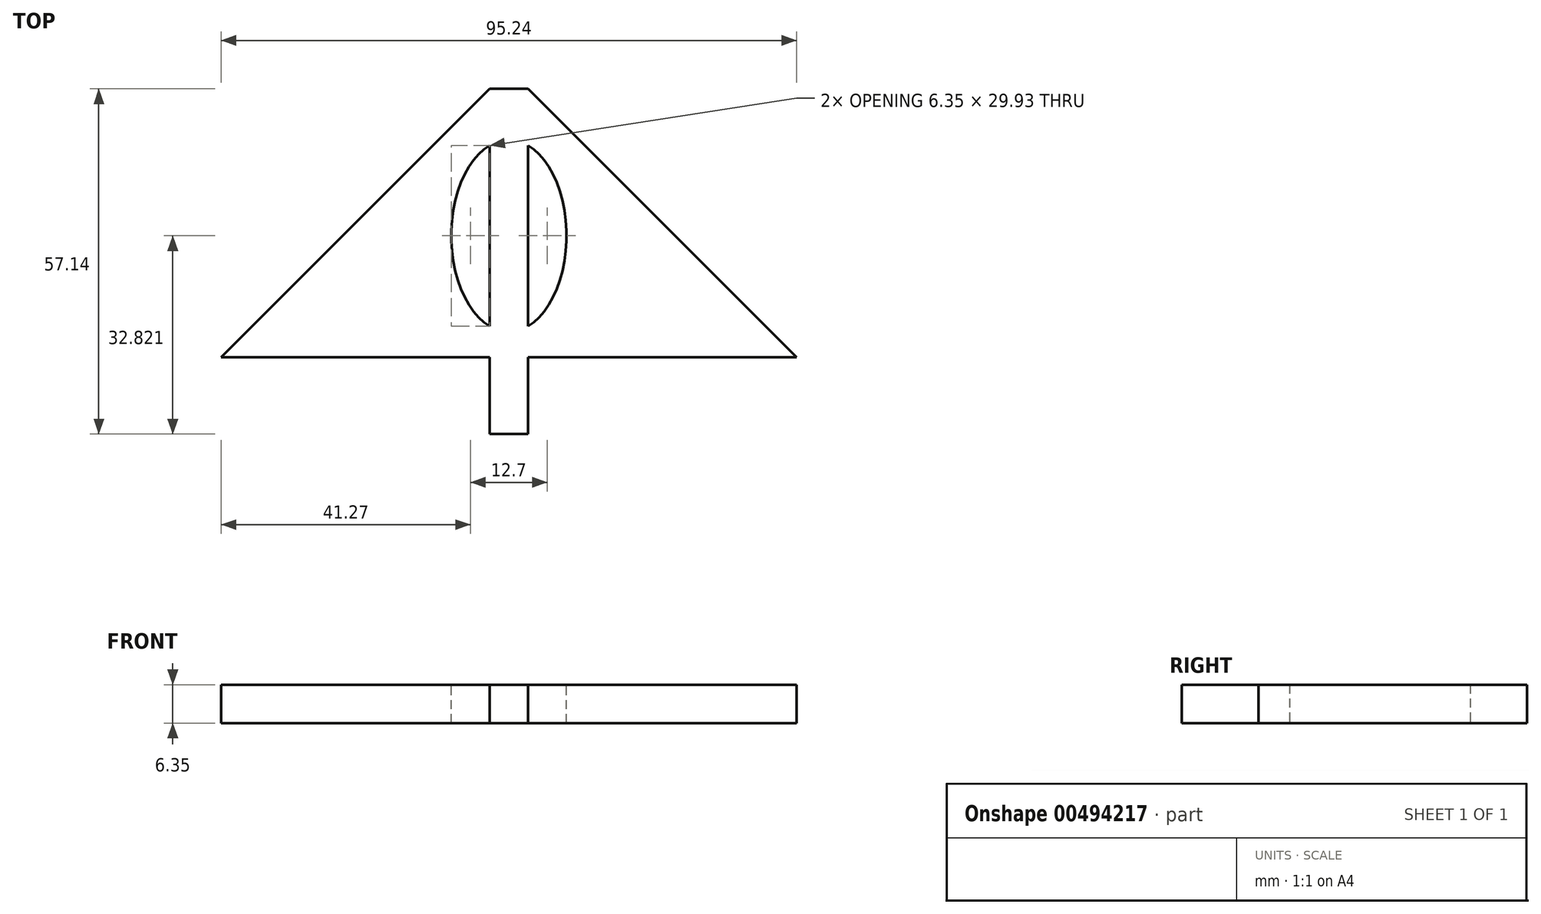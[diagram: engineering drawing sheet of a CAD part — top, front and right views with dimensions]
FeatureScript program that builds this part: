
annotation { "Feature Type Name" : "Feature", "Feature Type Description" : "" }
export const myFeature = defineFeature(function(context is Context, id is Id, definition is map)
    precondition{}
    {
        {
            var Q0;
            Q0=qCreatedBy(makeId("Top.planeOp"),FACE);
            var sketch = newSketch(context, id + "F0", { "sketchPlane" : qUnion([Q0])});
            skLineSegment(sketch, "E0.bottom", {"start": v(3.18, 28.58) * mm, "end": v(-3.17, 28.58) * mm});
            skLineSegment(sketch, "E0.top", {"start": v(3.17, -28.58) * mm, "end": v(-3.18, -28.58) * mm});
            skLineSegment(sketch, "E0.left", {"start": v(3.18, 28.58) * mm, "end": v(3.17, -28.58) * mm});
            skLineSegment(sketch, "E0.right", {"start": v(-3.17, 28.58) * mm, "end": v(-3.18, -28.58) * mm});
            skPoint(sketch, "E0.middle", {"position": v(0, 0) * mm});
            skLineSegment(sketch, "E1", {"start": v(-3.17, -15.87) * mm, "end": v(-47.62, -15.88) * mm});
            skLineSegment(sketch, "E2", {"start": v(-47.62, -15.88) * mm, "end": v(-3.17, 28.58) * mm});
            skLineSegment(sketch, "E3", {"start": v(3.18, -15.88) * mm, "end": v(47.62, -15.88) * mm});
            skLineSegment(sketch, "E4", {"start": v(47.62, -15.87) * mm, "end": v(3.18, 28.58) * mm});
            skEllipse(sketch, "E5", {"center": v(0, 4.25) * mm, "majorRadius": 15.88 * mm, "minorRadius": 9.53 * mm, "majorAxis": v(0, 1)});
            skSolve(sketch);
        }
        {
            var Q0;
            {var subQ0=sQuery(id+"F0.wireOp",EDGE,"E1");Q0=makeQuery(id+"F0.imprint","IMPRINT",FACE,{"disambiguationData":[TD([[makeQuery(id+"F0.imprint","IMPRINT",EDGE,{"derivedFrom":subQ0}),-1.0]])]});}
            var Q1;
            {var subQ4=sQuery(id+"F0.wireOp",EDGE,"E3");Q1=makeQuery(id+"F0.imprint","IMPRINT",FACE,{"disambiguationData":[TD([[makeQuery(id+"F0.imprint","IMPRINT",EDGE,{"derivedFrom":subQ4}),1.0]])]});}
            var Q2;
            {var subQ0=sQuery(id+"F0.wireOp",EDGE,"E5");var subQ1=sQuery(id+"F0.wireOp",EDGE,"E0.left");var subQ2=makeQuery(id+"F0.imprint","INTERSECT",VERTEX,{"disambiguationData":[OD(0.0)],"derivedFrom":[subQ1,subQ0]});Q2=makeQuery(id+"F0.imprint","IMPRINT",FACE,{"disambiguationData":[TD([[makeQuery(id+"F0.imprint","IMPRINT",EDGE,{"disambiguationData":[TD([[subQ2,-1.0]])],"derivedFrom":subQ1}),-1.0]])]});}
            var Q3;
            {var subQ0=sQuery(id+"F0.wireOp",EDGE,"E0.bottom");Q3=makeQuery(id+"F0.imprint","IMPRINT",FACE,{"disambiguationData":[TD([[makeQuery(id+"F0.imprint","IMPRINT",EDGE,{"derivedFrom":subQ0}),1.0]])]});}
            var Q4;
            {var subQ5=sQuery(id+"F0.wireOp",EDGE,"E0.top");Q4=makeQuery(id+"F0.imprint","IMPRINT",FACE,{"disambiguationData":[TD([[makeQuery(id+"F0.imprint","IMPRINT",EDGE,{"derivedFrom":subQ5}),-1.0]])]});}
            extrude(context, id + "F1", {"entities" : qUnion([Q0, Q1, Q2, Q3, Q4]), "depth" : 6.35 * mm});
        }
    });
